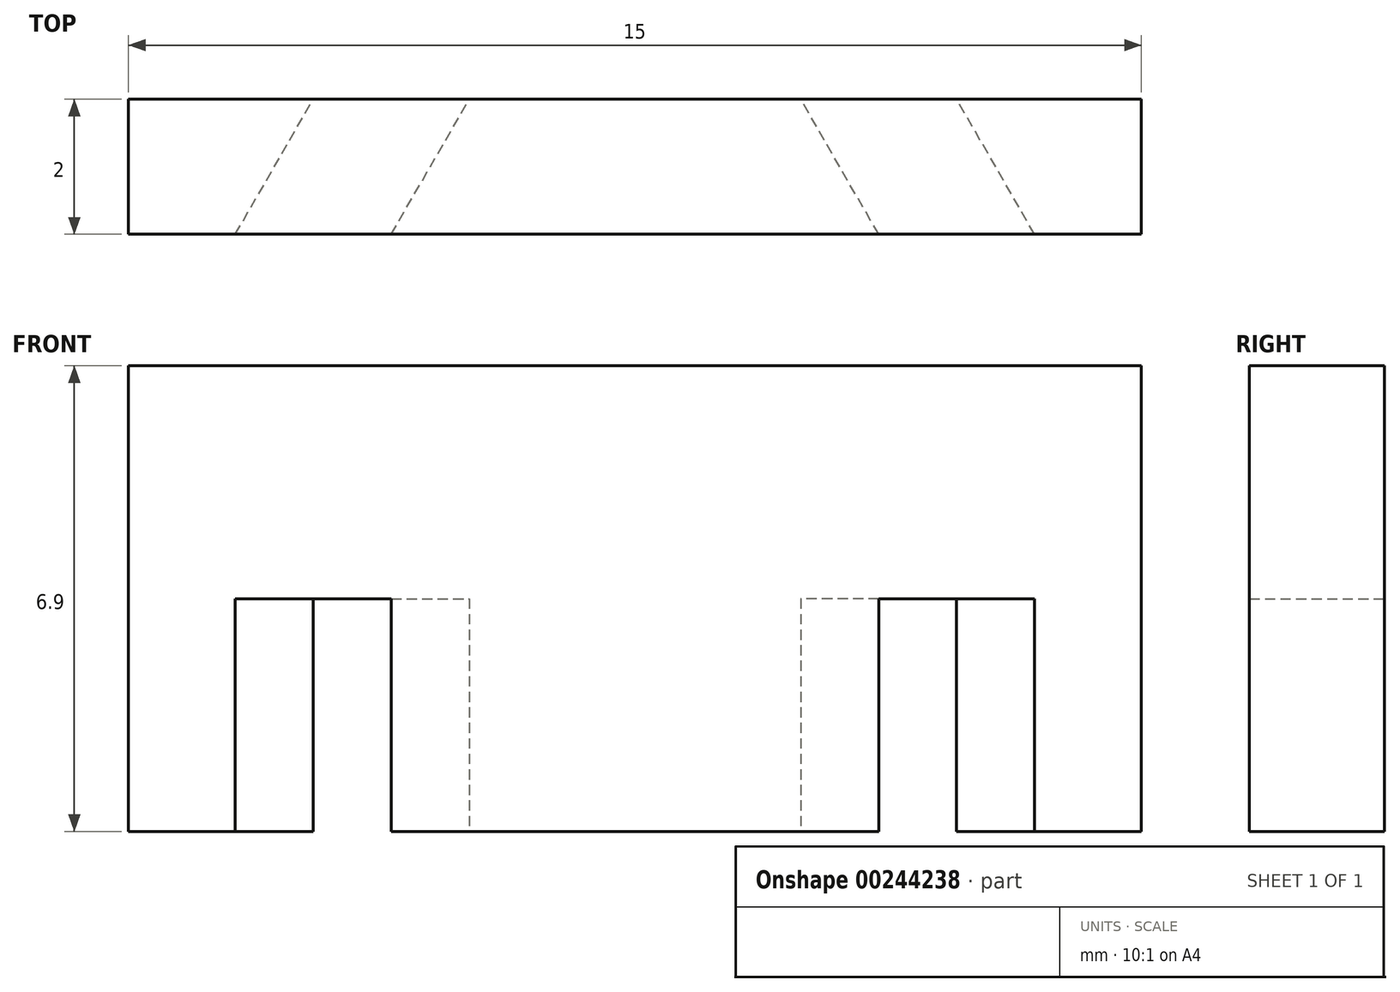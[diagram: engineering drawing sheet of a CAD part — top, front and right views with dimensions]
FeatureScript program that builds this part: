
annotation { "Feature Type Name" : "Feature", "Feature Type Description" : "" }
export const myFeature = defineFeature(function(context is Context, id is Id, definition is map)
    precondition{}
    {
        {
            var Q0;
            Q0=qCreatedBy(makeId("Top.planeOp"),FACE);
            var sketch = newSketch(context, id + "F0", { "sketchPlane" : qUnion([Q0])});
            skCircle(sketch, "E0.cCircle", {"center": v(0, 0) * mm, "radius": 11.25 * mm, "construction": true});
            skLineSegment(sketch, "E0.0", {"start": v(13, 0) * mm, "end": v(6.5, -11.25) * mm, "construction": true});
            skLineSegment(sketch, "E0.1", {"start": v(6.5, -11.25) * mm, "end": v(-6.5, -11.25) * mm, "construction": true});
            skLineSegment(sketch, "E0.2", {"start": v(-6.5, -11.25) * mm, "end": v(-13, 0) * mm, "construction": true});
            skLineSegment(sketch, "E0.3", {"start": v(-13, 0) * mm, "end": v(-6.5, 11.25) * mm, "construction": true});
            skLineSegment(sketch, "E0.4", {"start": v(-6.5, 11.25) * mm, "end": v(6.5, 11.25) * mm, "construction": true});
            skLineSegment(sketch, "E0.5", {"start": v(6.5, 11.25) * mm, "end": v(13, 0) * mm, "construction": true});
            skPoint(sketch, "E0.0.midPoint", {"position": v(9.74, -5.63) * mm});
            skLineSegment(sketch, "E1.0", {"start": v(-7.5, 8.25) * mm, "end": v(7.5, 8.25) * mm});
            skLineSegment(sketch, "E2.0", {"start": v(3.9, 9.75) * mm, "end": v(10.4, -1.5) * mm, "construction": true});
            skLineSegment(sketch, "E3.0", {"start": v(-10.38, -1.47) * mm, "end": v(-3.88, 9.78) * mm, "construction": true});
            skLineSegment(sketch, "E4.0", {"start": v(2.17, 8.75) * mm, "end": v(8.66, -2.5) * mm, "construction": true});
            skLineSegment(sketch, "E5.0", {"start": v(-8.64, -2.47) * mm, "end": v(-2.15, 8.78) * mm, "construction": true});
            skLineSegment(sketch, "E6.0", {"start": v(-7.5, 6.25) * mm, "end": v(7.5, 6.25) * mm});
            skLineSegment(sketch, "E7", {"start": v(7.5, 8.25) * mm, "end": v(7.5, 6.25) * mm});
            skLineSegment(sketch, "E8", {"start": v(-7.5, 6.25) * mm, "end": v(-7.5, 8.25) * mm});
            skSolve(sketch);
        }
        {
            var Q0;
            Q0 = qSketchRegion(id + "F0", true);
            extrude(context, id + "F1", {"entities" : qUnion([Q0]), "depth" : 6.9 * mm});
        }
        {
            var Q0;
            Q0=qCreatedBy(makeId("Top.planeOp"),FACE);
            var sketch = newSketch(context, id + "F2", { "sketchPlane" : qUnion([Q0])});
            skCircle(sketch, "E9.cCircle", {"center": v(0, 0) * mm, "radius": 11.25 * mm, "construction": true});
            skLineSegment(sketch, "E9.0", {"start": v(-6.5, 11.25) * mm, "end": v(6.5, 11.25) * mm, "construction": true});
            skLineSegment(sketch, "E9.1", {"start": v(6.5, 11.25) * mm, "end": v(13, 0) * mm, "construction": true});
            skLineSegment(sketch, "E9.2", {"start": v(13, 0) * mm, "end": v(6.5, -11.25) * mm, "construction": true});
            skLineSegment(sketch, "E9.3", {"start": v(6.5, -11.25) * mm, "end": v(-6.5, -11.25) * mm, "construction": true});
            skLineSegment(sketch, "E9.4", {"start": v(-6.5, -11.25) * mm, "end": v(-13, 0) * mm, "construction": true});
            skLineSegment(sketch, "E9.5", {"start": v(-13, 0) * mm, "end": v(-6.5, 11.25) * mm, "construction": true});
            skPoint(sketch, "E9.0.midPoint", {"position": v(0, 11.25) * mm});
            skLineSegment(sketch, "E10.0", {"start": v(-5.92, 6.25) * mm, "end": v(-4.76, 8.25) * mm});
            skLineSegment(sketch, "E11.0", {"start": v(-3.6, 6.25) * mm, "end": v(-2.45, 8.25) * mm});
            skLineSegment(sketch, "E12", {"start": v(-4.76, 8.25) * mm, "end": v(-2.45, 8.25) * mm});
            skLineSegment(sketch, "E13.0", {"start": v(-5.92, 6.25) * mm, "end": v(-3.6, 6.25) * mm});
            skLineSegment(sketch, "E14.MirrorCS", {"start": v(5.92, 6.25) * mm, "end": v(4.76, 8.25) * mm});
            skLineSegment(sketch, "E15.MirrorCS", {"start": v(4.76, 8.25) * mm, "end": v(2.45, 8.25) * mm});
            skLineSegment(sketch, "E16.MirrorCS", {"start": v(3.6, 6.25) * mm, "end": v(2.45, 8.25) * mm});
            skLineSegment(sketch, "E17.MirrorCS", {"start": v(5.92, 6.25) * mm, "end": v(3.6, 6.25) * mm});
            skSolve(sketch);
        }
        {
            var Q0;
            Q0 = qSketchRegion(id + "F2", true);
            extrude(context, id + "F3", {"entities" : qUnion([Q0]), "operationType" : NewBodyOperationType.REMOVE, "depth" : 3.45 * mm});
        }
    });
